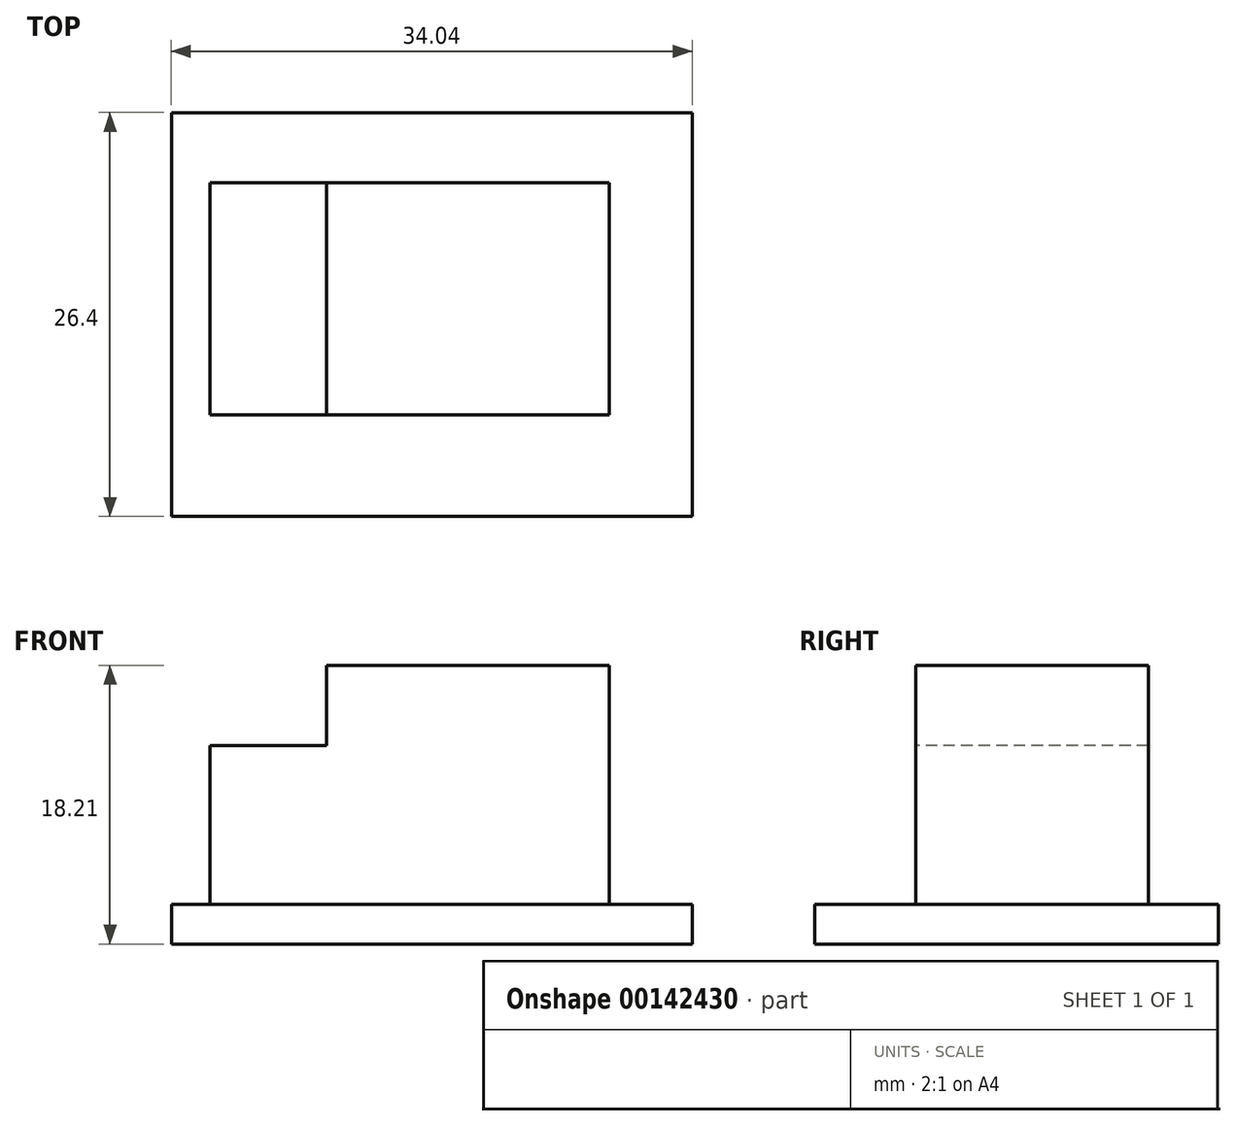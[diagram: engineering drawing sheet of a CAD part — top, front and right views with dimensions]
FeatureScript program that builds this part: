
annotation { "Feature Type Name" : "Feature", "Feature Type Description" : "" }
export const myFeature = defineFeature(function(context is Context, id is Id, definition is map)
    precondition{}
    {
        {
            var Q0;
            Q0=qCreatedBy(makeId("Top.planeOp"),FACE);
            var sketch = newSketch(context, id + "F0", { "sketchPlane" : qUnion([Q0])});
            skLineSegment(sketch, "E0.bottom", {"start": v(17.02, -13.2) * mm, "end": v(-17.02, -13.2) * mm});
            skLineSegment(sketch, "E0.top", {"start": v(17.02, 13.2) * mm, "end": v(-17.02, 13.2) * mm});
            skLineSegment(sketch, "E0.left", {"start": v(17.02, -13.2) * mm, "end": v(17.02, 13.2) * mm});
            skLineSegment(sketch, "E0.right", {"start": v(-17.02, -13.2) * mm, "end": v(-17.02, 13.2) * mm});
            skPoint(sketch, "E0.middle", {"position": v(0, 0) * mm});
            skSolve(sketch);
        }
        {
            var Q0;
            Q0 = qSketchRegion(id + "F0", true);
            extrude(context, id + "F1", {"entities" : qUnion([Q0]), "depth" : 2.6 * mm});
        }
        {
            var Q0;
            Q0=makeQuery(id+"F1.opExtrude","CAP_FACE",FACE,{"disambiguationData":[OSD([sQuery(id+"F0.wireOp",EDGE,"E0.bottom"),sQuery(id+"F0.wireOp",EDGE,"E0.top"),sQuery(id+"F0.wireOp",EDGE,"E0.left"),sQuery(id+"F0.wireOp",EDGE,"E0.right")])],"isStart":false});
            var sketch = newSketch(context, id + "F2", { "sketchPlane" : qUnion([Q0])});
            skLineSegment(sketch, "E1.bottom", {"start": v(11.6, -6.57) * mm, "end": v(-14.5, -6.57) * mm});
            skLineSegment(sketch, "E1.top", {"start": v(11.6, 8.62) * mm, "end": v(-14.5, 8.62) * mm});
            skLineSegment(sketch, "E1.left", {"start": v(11.6, -6.57) * mm, "end": v(11.6, 8.62) * mm});
            skLineSegment(sketch, "E1.right", {"start": v(-14.5, -6.57) * mm, "end": v(-14.5, 8.62) * mm});
            skPoint(sketch, "E1.middle", {"position": v(-1.45, 1.03) * mm});
            skSolve(sketch);
        }
        {
            var Q0;
            Q0 = qSketchRegion(id + "F2", true);
            extrude(context, id + "F3", {"entities" : qUnion([Q0]), "operationType" : NewBodyOperationType.ADD, "depth" : 15.62 * mm});
        }
        {
            var Q0;
            Q0=makeQuery(id+"F3.opExtrude","SWEPT_FACE",FACE,{"disambiguationData":[OSD([sQuery(id+"F2.wireOp",EDGE,"E1.bottom")])]});
            var sketch = newSketch(context, id + "F4", { "sketchPlane" : qUnion([Q0])});
            skLineSegment(sketch, "E2.bottom", {"start": v(-14.5, 12.98) * mm, "end": v(-6.88, 12.98) * mm});
            skLineSegment(sketch, "E2.top", {"start": v(-14.5, 18.21) * mm, "end": v(-6.88, 18.21) * mm});
            skLineSegment(sketch, "E2.left", {"start": v(-14.5, 12.98) * mm, "end": v(-14.5, 18.21) * mm});
            skLineSegment(sketch, "E2.right", {"start": v(-6.88, 12.98) * mm, "end": v(-6.88, 18.21) * mm});
            skSolve(sketch);
        }
        {
            var Q0;
            Q0 = qSketchRegion(id + "F4", true);
            extrude(context, id + "F5", {"entities" : qUnion([Q0]), "operationType" : NewBodyOperationType.REMOVE, "endBound" : BoundingType.THROUGH_ALL, "oppositeDirection" : true, "depth" : 25.4 * mm});
        }
    });
